# Revit family: NBS_Allermuir_OffcChrs_Folk_HighStool
name_source: partatom
category: Furniture
revit_build: Autodesk Revit 2018 (Build: 20190510_1515(x64)
units: mm (PartAtom-declared; Revit-internal decimal feet)

## family parameters
Always vertical = Yes
Cut with Voids When Loaded = No
Room Calculation Point = No
Shared = No
Work Plane-Based = No

## types (2) — shared parameters
AssetType = Movable
Category = Pr_40_50_12_57:Office chairs
CodePerformance = BS EN 16139 level 1
Color = Off black, White, Crayon grey, Pistachio, Seattle green, Aubergine
DurationUnit = year
ExpectedLife = 10
Finish = Off-Black powder coat, White powder coat, Crayon Grey powder coat, Pistachio powder coat, Seattle Green powder coat, Aubergine powder coat, Off-Black plastic, White plastic, Crayon Grey plastic, Pistachio plastic, Seattle Green plastic, Aubergine plastic, Clear Beech, Clear Oak, American Cherry, American Walnut, Dark Walnut, Wenge, Off-Black colour wash, White colour wash, Crayon Grey colour wash, Pistachio colour wash, Seattle Green colour wash, Aubergine colour wash
FrameFinish = Off black, White, Crayon grey, Pistachio, Seattle green, Aubergine
FrameMaterial = NBS_Allermuir_Aluminium_BlackPowderCoat
IfcExportAs = IfcFurnitureType
IfcExportType = STOOL
IsBuiltIn = No
LegMaterial = NBS_Allermuir_Beech_ClearFinish
ManufacturerName = Allermuir
ManufacturerURL = www.allermuir.co.uk
Material = Solid Wood, Polypropylene, Aluminium Casting
ModelReference = Folk_HighStool
NBSCertification = www.nationalbimlibrary.com/cert/cexzx3zn
NBSDescription = Office chairs
NBSReference = 45-35-20/330
NominalDepth = 520 mm
NominalHeight = 1100 mm
NominalLength = 485 mm  [stored 1.59121 ft]
NominalWidth = 485 mm  [stored 1.59121 ft]
ProductInformation = https://www.allermuir.com
SeatDepth = 435 mm
SeatHeight = 750 mm
SeatWidth = 455 mm
SeatingHeight = 750 mm  [stored 2.46063 ft]
Size = 520 x 1100 x 485 mm
Status = UNSET
Style = Stool
SustainabilityPerformance = 99% recyclable
Uniclass2015Code = Pr_40_50_12_57
Uniclass2015Title = Office chairs
Uniclass2015Version = Products v1.15
Version = 1
WarrantyDescription = Allermuir warrant that its manufactured products are free from manufacturing defects - in materials or workmanship - for a period of five (5) years. , Allermuir will repair, or replace (at Allermuir's sole discretion) with comparable free of charge materials / components, any product / component which fails under normal use in a single shift environment, as a result of a defect in the materials and/ or workmanship
WarrantyDurationParts = 5
WarrantyDurationUnit = year
WoodStains = Clear Oak, American Cherry, American Walnut, Dark Walnut, Wenge
zero-valued in all types: HighestSeatingHeight, LowestSeatingHeight

## per-type parameters (varying)
| type | BIMObjectName | Description | Features | ModelNumber | Name | SeatMaterial |
| Folk_HighStool_FLK301 | NBS_Allermuir_OfficeChairs_Folk_HighStool_FLK301 | Stool - Wood seat and back | Beech ply seat with a clear finish, Beech ply back with a clear finish, Cast Aluminium frame finished in Off-Black powder coat, Solid Beech legs with a clear finish, Plastic glides, Footrest finished in Off-Black powdercoat, Footrest protector, Cast Aluminium frame available in White, Crayon Grey, Pistachio, Aubergine or Seattle Green powdercoat, Beech ply seat, back and solid Beech legs available in Off-Black, White, Crayon Grey, Pistachio, Aubergine and Seattle Green colourwash or stained, Oak ply seat, back and solid Oak legs with a clear finish, Oak ply seat and back with a clear finish, Plastic glides with felt | FLK301 | OfficeChairs_FLK301_Folk_Allermuir | NBS_Allermuir_Beech_ClearFinish |
| Folk_HighStool_FLK303 | NBS_Allermuir_OfficeChairs_Folk_HighStool_FLK303 | Stool - Plastic seat and back | Plastic seat — Colour: Off-Black, Plastic back — Colour: Off-Black, Cast Aluminium frame finished in Off-Black powder coat, Solid Beech legs with a clear finish, Plastic glides, Footrest finished in Off-Black powdercoat, Footrest protector, Cast Aluminium frame available in White, Crayon Grey, Pistachio, Aubergine or Seattle Green powdercoat, Plastic seat and back available in White, Crayon Grey, Pistachio, Aubergine or Seattle Green, Solid Beech legs available in Off-Black, White, Crayon Grey, Pistachio, Aubergine and Seattle Green colourwash or stained, Solid Oak legs with a clear finish, Plastic glides with felt | FLK303 | OfficeChairs_FLK303_Folk_Allermuir | NBS_Allermuir_Plastic_Black |

note: [stored X ft] marks values corroborated as IEEE doubles in the binary element streams (Revit-internal decimal feet)

## geometry (parser evidence)
native form markers: Sweep x5
no freeform markers — native parametric forms only
